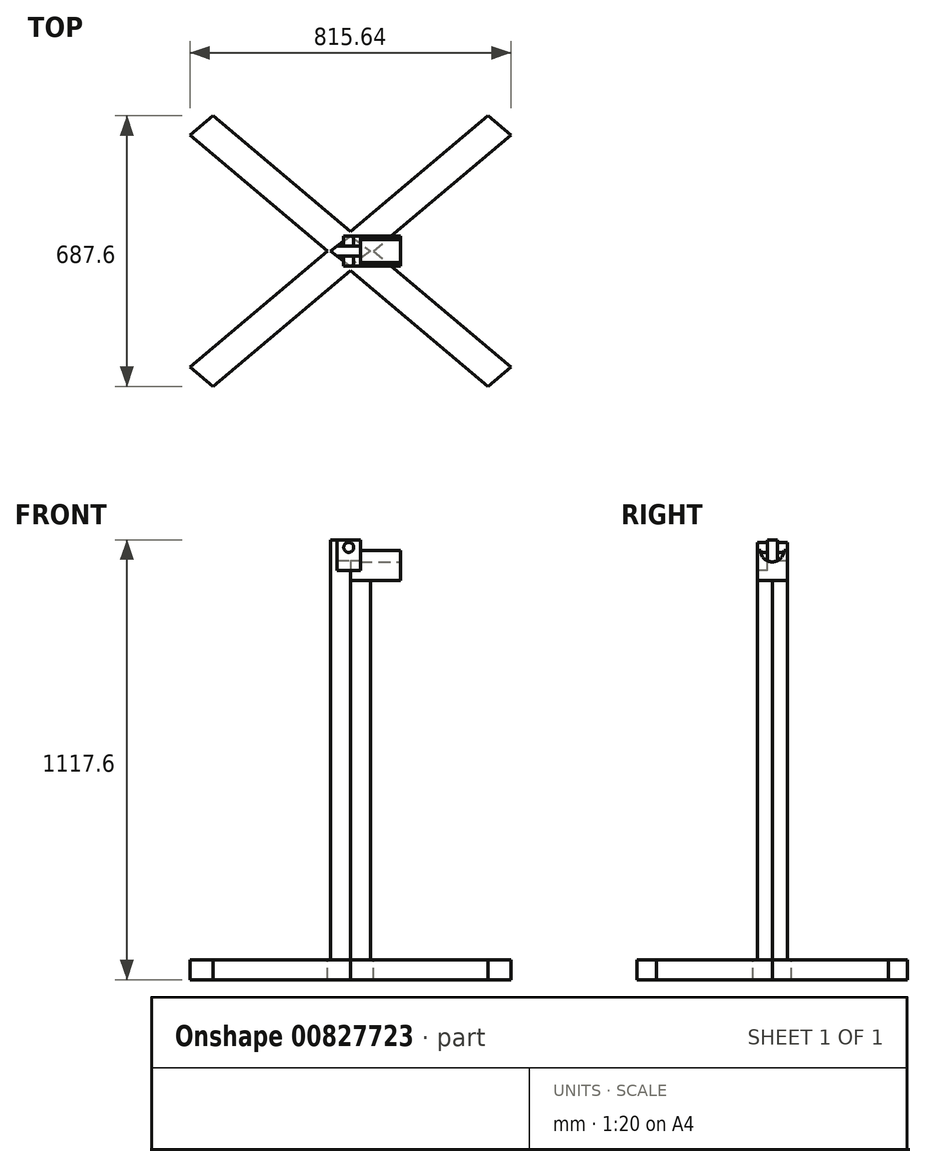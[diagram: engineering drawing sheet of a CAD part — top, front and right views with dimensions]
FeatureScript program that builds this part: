
annotation { "Feature Type Name" : "Feature", "Feature Type Description" : "" }
export const myFeature = defineFeature(function(context is Context, id is Id, definition is map)
    precondition{}
    {
        {
            var Q0;
            Q0=qCreatedBy(makeId("Top.planeOp"),FACE);
            var sketch = newSketch(context, id + "F0", { "sketchPlane" : qUnion([Q0])});
            skPoint(sketch, "E0.middle", {"position": v(0, 0) * mm});
            skLineSegment(sketch, "E1", {"start": v(282.37, -288.57) * mm, "end": v(-67.19, 6.12) * mm});
            skLineSegment(sketch, "E2", {"start": v(-475.01, 349.91) * mm, "end": v(-416.75, 399.03) * mm});
            skLineSegment(sketch, "E3", {"start": v(-416.75, 399.03) * mm, "end": v(-67.19, 104.34) * mm});
            skLineSegment(sketch, "E4", {"start": v(-475.01, -239.45) * mm, "end": v(-416.75, -288.57) * mm});
            skLineSegment(sketch, "E5", {"start": v(-416.75, -288.57) * mm, "end": v(-67.19, 6.12) * mm});
            skLineSegment(sketch, "E6", {"start": v(340.63, 349.91) * mm, "end": v(282.37, 399.03) * mm});
            skLineSegment(sketch, "E7", {"start": v(282.37, 399.03) * mm, "end": v(-67.19, 104.34) * mm});
            skLineSegment(sketch, "E8", {"start": v(282.37, -288.57) * mm, "end": v(340.63, -239.45) * mm});
            skLineSegment(sketch, "E9.trimOffspring", {"start": v(-8.93, 55.23) * mm, "end": v(340.63, -239.45) * mm});
            skLineSegment(sketch, "E10.trimOffspring", {"start": v(-125.45, 55.23) * mm, "end": v(-475.01, -239.45) * mm});
            skLineSegment(sketch, "E11.trimOffspring", {"start": v(-125.45, 55.23) * mm, "end": v(-475.01, 349.91) * mm});
            skLineSegment(sketch, "E12.trimOffspring", {"start": v(-8.93, 55.23) * mm, "end": v(340.63, 349.91) * mm});
            skSolve(sketch);
        }
        {
            var Q0;
            Q0=qSketchRegion(id+"F0",true);
            extrude(context, id + "F1", {"entities" : qUnion([Q0]), "oppositeDirection" : true, "depth" : 50.8 * mm, "offsetDistance" : 25.4 * mm});
        }
        {
            var Q0;
            Q0=makeQuery(id+"F1.opExtrude","CAP_FACE",FACE,{"disambiguationData":[OSD([sQuery(id+"F0.wireOp",EDGE,"E1"),sQuery(id+"F0.wireOp",EDGE,"E2"),sQuery(id+"F0.wireOp",EDGE,"E3"),sQuery(id+"F0.wireOp",EDGE,"E4"),sQuery(id+"F0.wireOp",EDGE,"E5"),sQuery(id+"F0.wireOp",EDGE,"E6"),sQuery(id+"F0.wireOp",EDGE,"E7"),sQuery(id+"F0.wireOp",EDGE,"E8"),sQuery(id+"F0.wireOp",EDGE,"E9.trimOffspring"),sQuery(id+"F0.wireOp",EDGE,"E10.trimOffspring"),sQuery(id+"F0.wireOp",EDGE,"E11.trimOffspring"),sQuery(id+"F0.wireOp",EDGE,"E12.trimOffspring")])],"isStart":true});
            var sketch = newSketch(context, id + "F2", { "sketchPlane" : qUnion([Q0])});
            skLineSegment(sketch, "E13", {"start": v(-125.45, 55.23) * mm, "end": v(-8.93, 55.23) * mm, "construction": true});
            skLineSegment(sketch, "E14", {"start": v(-67.19, 104.34) * mm, "end": v(-67.19, 6.12) * mm, "construction": true});
            skPoint(sketch, "E15.middle", {"position": v(-67.19, 55.23) * mm});
            skLineSegment(sketch, "E16", {"start": v(-117.99, 55.23) * mm, "end": v(-67.19, 93.33) * mm});
            skLineSegment(sketch, "E17", {"start": v(-67.19, 93.33) * mm, "end": v(-16.39, 55.23) * mm});
            skLineSegment(sketch, "E18", {"start": v(-16.39, 55.23) * mm, "end": v(-67.19, 17.13) * mm});
            skLineSegment(sketch, "E19", {"start": v(-67.19, 17.13) * mm, "end": v(-117.99, 55.23) * mm});
            skSolve(sketch);
        }
        {
            var Q0;
            {var subQ0=sQuery(id+"F2.wireOp",EDGE,"wgdWIPvC-I4hR-T0Zt-xnxe-Nl3ozaKQzP4W");var subQ1=makeQuery(id+"F2.imprint","INTERSECT",VERTEX,{"derivedFrom":[makeQuery(id+"F1.opExtrude","CAP_EDGE",EDGE,{"disambiguationData":[OSD([sQuery(id+"F0.wireOp",EDGE,"E1")])],"isStart":true}),makeQuery(id+"F1.opExtrude","CAP_EDGE",EDGE,{"disambiguationData":[OSD([sQuery(id+"F0.wireOp",EDGE,"E5")])],"isStart":true}),subQ0]});Q0=makeQuery(id+"F2.imprint","IMPRINT",FACE,{"disambiguationData":[TD([[makeQuery(id+"F2.imprint","IMPRINT",EDGE,{"disambiguationData":[TD([[subQ1,1.0]])],"derivedFrom":subQ0}),1.0]])]});}
            var Q1;
            Q1=makeQuery(id+"F2.imprint","IMPRINT",FACE,{"disambiguationData":[TD([[makeQuery(id+"F2.imprint","IMPRINT",EDGE,{"derivedFrom":sQuery(id+"F2.wireOp",EDGE,"VLmX2QcA-QAkb-Bhdo-7lbi-0TtQg2hfHBJQ")}),-1.0]])]});
            var Q2;
            Q2=makeQuery(id+"F2.imprint","IMPRINT",FACE,{"disambiguationData":[TD([[makeQuery(id+"F2.imprint","IMPRINT",EDGE,{"derivedFrom":sQuery(id+"F2.wireOp",EDGE,"E16")}),-1.0]])]});
            extrude(context, id + "F3", {"entities" : qUnion([Q0, Q1, Q2]), "operationType" : NewBodyOperationType.ADD, "depth" : 1066.8 * mm, "offsetDistance" : 25.4 * mm});
        }
        {
            var Q0;
            Q0=makeQuery(id+"F3.opExtrude","CAP_FACE",FACE,{"disambiguationData":[OSD([sQuery(id+"F2.wireOp",EDGE,"E16"),sQuery(id+"F2.wireOp",EDGE,"E17"),sQuery(id+"F2.wireOp",EDGE,"E18"),sQuery(id+"F2.wireOp",EDGE,"E19")])],"isStart":false});
            var sketch = newSketch(context, id + "F4", { "sketchPlane" : qUnion([Q0])});
            skLineSegment(sketch, "E20.top", {"start": v(-28.53, 103.17) * mm, "end": v(-104.72, 103.17) * mm});
            skLineSegment(sketch, "E20.left", {"start": v(-28.53, 67.93) * mm, "end": v(-28.53, 103.17) * mm});
            skLineSegment(sketch, "E20.right", {"start": v(-104.72, 67.93) * mm, "end": v(-104.72, 103.17) * mm});
            skLineSegment(sketch, "E21.bottom", {"start": v(-104.45, 42.53) * mm, "end": v(-29.62, 42.53) * mm});
            skLineSegment(sketch, "E21.top", {"start": v(-104.45, 3.33) * mm, "end": v(-29.62, 3.33) * mm});
            skLineSegment(sketch, "E21.left", {"start": v(-104.45, 42.53) * mm, "end": v(-104.45, 3.33) * mm});
            skLineSegment(sketch, "E21.right", {"start": v(-29.62, 42.53) * mm, "end": v(-29.62, 3.33) * mm});
            skLineSegment(sketch, "E22", {"start": v(-117.99, 55.23) * mm, "end": v(-16.39, 55.23) * mm, "construction": true});
            skLineSegment(sketch, "E23", {"start": v(-104.72, 67.93) * mm, "end": v(-28.53, 67.93) * mm});
            skSolve(sketch);
        }
        {
            var Q0;
            {var subQ0=sQuery(id+"F4.wireOp",EDGE,"E21.bottom");var subQ1=makeQuery(id+"F3.opExtrude","CAP_EDGE",EDGE,{"disambiguationData":[OSD([sQuery(id+"F2.wireOp",EDGE,"E19")])],"isStart":false});var subQ2=makeQuery(id+"F4.imprint","INTERSECT",VERTEX,{"derivedFrom":[subQ1,subQ0]});Q0=makeQuery(id+"F4.imprint","IMPRINT",FACE,{"disambiguationData":[TD([[makeQuery(id+"F4.imprint","IMPRINT",EDGE,{"disambiguationData":[TD([[subQ2,-1.0]])],"derivedFrom":subQ0}),-1.0]])]});}
            var Q1;
            {var subQ0=sQuery(id+"F4.wireOp",EDGE,"E20.bottom");var subQ1=makeQuery(id+"F3.opExtrude","CAP_EDGE",EDGE,{"disambiguationData":[OSD([sQuery(id+"F2.wireOp",EDGE,"E17")])],"isStart":false});var subQ2=makeQuery(id+"F4.imprint","INTERSECT",VERTEX,{"derivedFrom":[subQ1,subQ0]});Q1=makeQuery(id+"F4.imprint","IMPRINT",FACE,{"disambiguationData":[TD([[makeQuery(id+"F4.imprint","IMPRINT",EDGE,{"disambiguationData":[TD([[subQ2,-1.0]])],"derivedFrom":subQ0}),-1.0]])]});}
            var Q2;
            {var subQ0=sQuery(id+"F4.wireOp",EDGE,"E23");var subQ1=makeQuery(id+"F3.opExtrude","CAP_EDGE",EDGE,{"disambiguationData":[OSD([sQuery(id+"F2.wireOp",EDGE,"E16")])],"isStart":false});var subQ2=makeQuery(id+"F4.imprint","INTERSECT",VERTEX,{"derivedFrom":[subQ1,subQ0]});Q2=makeQuery(id+"F4.imprint","IMPRINT",FACE,{"disambiguationData":[TD([[makeQuery(id+"F4.imprint","IMPRINT",EDGE,{"disambiguationData":[TD([[subQ2,-1.0]])],"derivedFrom":subQ0}),1.0]])]});}
            extrude(context, id + "F5", {"entities" : qUnion([Q0, Q1, Q2]), "operationType" : NewBodyOperationType.REMOVE, "oppositeDirection" : true, "depth" : 26.67 * mm, "offsetDistance" : 25.4 * mm});
        }
        {
            var Q0;
            Q0=makeQuery(id+"F5.boolean.opBoolean","COPY",FACE,{"derivedFrom":makeQuery(id+"F5.opExtrude","CAP_FACE",FACE,{"disambiguationData":[OSD([sQuery(id+"F2.wireOp",EDGE,"E16"),sQuery(id+"F2.wireOp",EDGE,"E17"),sQuery(id+"F4.wireOp",EDGE,"E23")])],"isStart":false})});
            var sketch = newSketch(context, id + "F6", { "sketchPlane" : qUnion([Q0])});
            skLineSegment(sketch, "E24.0", {"start": v(-67.19, 93.33) * mm, "end": v(-33.32, 67.93) * mm});
            skLineSegment(sketch, "E25.0", {"start": v(-33.32, 67.93) * mm, "end": v(-16.39, 55.23) * mm});
            skLineSegment(sketch, "E26.0", {"start": v(-16.39, 55.23) * mm, "end": v(-33.32, 42.53) * mm});
            skLineSegment(sketch, "E27.0", {"start": v(-33.32, 42.53) * mm, "end": v(-67.19, 17.13) * mm});
            skLineSegment(sketch, "E28.bottom", {"start": v(-67.19, 93.33) * mm, "end": v(59.81, 93.33) * mm});
            skLineSegment(sketch, "E28.top", {"start": v(-67.19, 17.13) * mm, "end": v(59.81, 17.13) * mm});
            skLineSegment(sketch, "E28.right", {"start": v(59.81, 93.33) * mm, "end": v(59.81, 17.13) * mm});
            skSolve(sketch);
        }
        {
            var Q0;
            Q0=makeQuery(id+"F6.imprint","IMPRINT",FACE,{"disambiguationData":[TD([[makeQuery(id+"F6.imprint","IMPRINT",EDGE,{"derivedFrom":sQuery(id+"F6.wireOp",EDGE,"E24.0")}),1.0]])]});
            extrude(context, id + "F7", {"entities" : qUnion([Q0]), "operationType" : NewBodyOperationType.ADD, "oppositeDirection" : true, "depth" : 76.2 * mm, "offsetDistance" : 25.4 * mm});
        }
        {
            var Q0;
            Q0=makeQuery(id+"F7.opExtrude","SWEPT_FACE",FACE,{"disambiguationData":[OSD([sQuery(id+"F6.wireOp",EDGE,"E28.right")])]});
            var sketch = newSketch(context, id + "F8", { "sketchPlane" : qUnion([Q0])});
            skCircle(sketch, "E29", {"center": v(55.23, 1040.13) * mm, "radius": 29.21 * mm});
            skSolve(sketch);
        }
        {
            var Q0;
            Q0=qSketchRegion(id+"F8",true);
            extrude(context, id + "F9", {"entities" : qUnion([Q0]), "operationType" : NewBodyOperationType.REMOVE, "oppositeDirection" : true, "depth" : 101.6 * mm, "offsetDistance" : 25.4 * mm});
        }
        {
            var Q0;
            Q0=makeQuery(id+"F3.opExtrude","CAP_FACE",FACE,{"disambiguationData":[OSD([sQuery(id+"F2.wireOp",EDGE,"E16"),sQuery(id+"F2.wireOp",EDGE,"E17"),sQuery(id+"F2.wireOp",EDGE,"E18"),sQuery(id+"F2.wireOp",EDGE,"E19")])],"isStart":false});
            var sketch = newSketch(context, id + "F10", { "sketchPlane" : qUnion([Q0])});
            skLineSegment(sketch, "E30.0", {"start": v(-41.79, 67.93) * mm, "end": v(-33.32, 67.93) * mm});
            skLineSegment(sketch, "E31.0", {"start": v(-33.32, 67.93) * mm, "end": v(-16.39, 55.23) * mm});
            skLineSegment(sketch, "E32.0", {"start": v(-16.39, 55.23) * mm, "end": v(-33.32, 42.53) * mm});
            skLineSegment(sketch, "E33.0", {"start": v(-41.79, 42.53) * mm, "end": v(-33.32, 42.53) * mm});
            skLineSegment(sketch, "E34", {"start": v(-41.79, 67.93) * mm, "end": v(-41.79, 42.53) * mm});
            skPoint(sketch, "E35.orphan", {"position": v(-101.06, 67.93) * mm});
            skPoint(sketch, "E36.orphan", {"position": v(-101.06, 42.53) * mm});
            skPoint(sketch, "E37.0.end.orphan", {"position": v(-41.79, 84.44) * mm});
            skSolve(sketch);
        }
        {
            var Q0;
            Q0=makeQuery(id+"F10.imprint","IMPRINT",FACE,{"disambiguationData":[TD([[makeQuery(id+"F10.imprint","IMPRINT",EDGE,{"derivedFrom":sQuery(id+"F10.wireOp",EDGE,"E30.0")}),-1.0]])]});
            var Q1;
            {var subQ0=sQuery(id+"F10.wireOp",EDGE,"E33.0");Q1=makeQuery(id+"F10.imprint","IMPRINT",FACE,{"disambiguationData":[TD([[makeQuery(id+"F10.imprint","IMPRINT",EDGE,{"derivedFrom":subQ0}),1.0]])]});}
            extrude(context, id + "F11", {"entities" : qUnion([Q0, Q1]), "operationType" : NewBodyOperationType.REMOVE, "endBound" : BoundingType.UP_TO_NEXT, "oppositeDirection" : true, "depth" : 50.8 * mm, "offsetDistance" : 25.4 * mm});
        }
        {
            var Q0;
            Q0=makeQuery(id+"F9.boolean.opBoolean","COPY",FACE,{"derivedFrom":makeQuery(id+"F9.opExtrude","CAP_FACE",FACE,{"disambiguationData":[OSD([sQuery(id+"F8.wireOp",EDGE,"E29")])],"isStart":false})});
            var sketch = newSketch(context, id + "F12", { "sketchPlane" : qUnion([Q0])});
            skLineSegment(sketch, "E38.0", {"start": v(26.02, 1040.13) * mm, "end": v(42.53, 1040.13) * mm});
            skLineSegment(sketch, "E39.0", {"start": v(67.93, 1040.13) * mm, "end": v(84.44, 1040.13) * mm});
            skArc(sketch, "E40.0", {"start": v(26.02, 1040.13) * mm, "mid": v(30.49, 1024.6) * mm, "end": v(42.53, 1013.83) * mm});
            skLineSegment(sketch, "E41", {"start": v(42.53, 1040.13) * mm, "end": v(42.53, 1013.83) * mm});
            skLineSegment(sketch, "E42", {"start": v(67.93, 1040.13) * mm, "end": v(67.93, 1013.83) * mm});
            skArc(sketch, "E43.trimOffspring", {"start": v(67.93, 1013.83) * mm, "mid": v(79.97, 1024.6) * mm, "end": v(84.44, 1040.13) * mm});
            skSolve(sketch);
        }
        {
            var Q0;
            Q0=qSketchRegion(id+"F12",true);
            extrude(context, id + "F13", {"entities" : qUnion([Q0]), "operationType" : NewBodyOperationType.REMOVE, "endBound" : BoundingType.UP_TO_NEXT, "oppositeDirection" : true, "depth" : 25.4 * mm, "offsetDistance" : 25.4 * mm});
        }
        {
            var Q0;
            Q0=makeQuery(id+"F7.opExtrude","SWEPT_FACE",FACE,{"disambiguationData":[OSD([sQuery(id+"F6.wireOp",EDGE,"E28.top")])]});
            var sketch = newSketch(context, id + "F14", { "sketchPlane" : qUnion([Q0])});
            skLineSegment(sketch, "E44.0", {"start": v(-67.19, 1040.13) * mm, "end": v(-41.79, 1040.13) * mm});
            skPoint(sketch, "E45.orphan", {"position": v(59.81, 1040.13) * mm});
            skPoint(sketch, "E46.orphan", {"position": v(-41.79, 1066.8) * mm});
            skLineSegment(sketch, "E47", {"start": v(-67.19, 1040.13) * mm, "end": v(-101.06, 1040.13) * mm});
            skPoint(sketch, "E48.orphan", {"position": v(-101.06, 1066.8) * mm});
            skLineSegment(sketch, "E49.top", {"start": v(-101.06, 989.33) * mm, "end": v(-41.79, 989.33) * mm});
            skLineSegment(sketch, "E50", {"start": v(-101.06, 989.33) * mm, "end": v(-101.06, 1040.13) * mm});
            skLineSegment(sketch, "E51", {"start": v(-41.79, 989.33) * mm, "end": v(-41.79, 1040.13) * mm});
            skSolve(sketch);
        }
        {
            var Q0;
            {var subQ0=sQuery(id+"F14.wireOp",EDGE,"91e3f64d-cfc5-48aa-956f-56200beb85da.0");Q0=makeQuery(id+"F14.imprint","IMPRINT",FACE,{"disambiguationData":[TD([[makeQuery(id+"F14.imprint","IMPRINT",EDGE,{"derivedFrom":subQ0}),-1.0]])]});}
            var Q1;
            {var subQ0=sQuery(id+"F14.wireOp",EDGE,"3b4ab840-8c4a-4b07-9c90-480e8c33c28e.0");Q1=makeQuery(id+"F14.imprint","IMPRINT",FACE,{"disambiguationData":[TD([[makeQuery(id+"F14.imprint","IMPRINT",EDGE,{"derivedFrom":subQ0}),1.0]])]});}
            var Q2;
            {var subQ0=sQuery(id+"F14.wireOp",EDGE,"E47");Q2=makeQuery(id+"F14.imprint","IMPRINT",FACE,{"disambiguationData":[TD([[makeQuery(id+"F14.imprint","IMPRINT",EDGE,{"derivedFrom":subQ0}),1.0]])]});}
            var Q3;
            {var subQ0=sQuery(id+"F14.wireOp",EDGE,"E44.0");Q3=makeQuery(id+"F14.imprint","IMPRINT",FACE,{"disambiguationData":[TD([[makeQuery(id+"F14.imprint","IMPRINT",EDGE,{"derivedFrom":subQ0}),-1.0]])]});}
            var Q4;
            Q4=makeQuery(id+"F13.boolean.opBoolean","MERGE",FACE,{"derivedFrom":[makeQuery(id+"F5.boolean.opBoolean","COPY",FACE,{"derivedFrom":makeQuery(id+"F5.opExtrude","SWEPT_FACE",FACE,{"disambiguationData":[OSD([sQuery(id+"F4.wireOp",EDGE,"E21.bottom")])]})}),makeQuery(id+"F13.opExtrude","SWEPT_FACE",FACE,{"disambiguationData":[OSD([sQuery(id+"F12.wireOp",EDGE,"E41")])]})]});
            extrude(context, id + "F15", {"entities" : qUnion([Q0, Q1, Q2, Q3]), "operationType" : NewBodyOperationType.REMOVE, "oppositeDirection" : true, "depth" : 25.4 * mm, "endBoundEntityFace" : qUnion([Q4]), "offsetDistance" : 25.4 * mm});
        }
        {
            var Q0;
            Q0=makeQuery(id+"F7.opExtrude","SWEPT_FACE",FACE,{"disambiguationData":[OSD([sQuery(id+"F6.wireOp",EDGE,"E28.bottom")])]});
            var sketch = newSketch(context, id + "F16", { "sketchPlane" : qUnion([Q0])});
            skLineSegment(sketch, "E52.0", {"start": v(41.79, 1013.83) * mm, "end": v(41.79, 1040.13) * mm});
            skLineSegment(sketch, "E53.0", {"start": v(101.06, 1013.83) * mm, "end": v(41.79, 1013.83) * mm});
            skLineSegment(sketch, "E54.0", {"start": v(101.06, 1013.83) * mm, "end": v(101.06, 1040.13) * mm});
            skLineSegment(sketch, "E55.0", {"start": v(67.19, 1040.13) * mm, "end": v(41.79, 1040.13) * mm});
            skLineSegment(sketch, "E56", {"start": v(67.19, 1040.13) * mm, "end": v(101.06, 1040.13) * mm});
            skPoint(sketch, "E57.orphan", {"position": v(41.79, 1066.8) * mm});
            skPoint(sketch, "E58.orphan", {"position": v(101.06, 1066.8) * mm});
            skPoint(sketch, "E59.orphan", {"position": v(-59.81, 1040.13) * mm});
            skSolve(sketch);
        }
        {
            var Q0;
            {var subQ0=sQuery(id+"F16.wireOp",EDGE,"E54.0");Q0=makeQuery(id+"F16.imprint","IMPRINT",FACE,{"disambiguationData":[TD([[makeQuery(id+"F16.imprint","IMPRINT",EDGE,{"derivedFrom":subQ0}),1.0]])]});}
            var Q1;
            {var subQ0=sQuery(id+"F16.wireOp",EDGE,"E52.0");Q1=makeQuery(id+"F16.imprint","IMPRINT",FACE,{"disambiguationData":[TD([[makeQuery(id+"F16.imprint","IMPRINT",EDGE,{"derivedFrom":subQ0}),-1.0]])]});}
            extrude(context, id + "F17", {"entities" : qUnion([Q0, Q1]), "operationType" : NewBodyOperationType.REMOVE, "oppositeDirection" : true, "depth" : 25.4 * mm, "offsetDistance" : 25.4 * mm});
        }
        {
            var Q0;
            Q0=makeQuery(id+"F13.boolean.opBoolean","MERGE",FACE,{"derivedFrom":[makeQuery(id+"F5.boolean.opBoolean","COPY",FACE,{"derivedFrom":makeQuery(id+"F5.opExtrude","SWEPT_FACE",FACE,{"disambiguationData":[OSD([sQuery(id+"F4.wireOp",EDGE,"E21.bottom")])]})}),makeQuery(id+"F13.opExtrude","SWEPT_FACE",FACE,{"disambiguationData":[OSD([sQuery(id+"F12.wireOp",EDGE,"E41")])]})]});
            var sketch = newSketch(context, id + "F18", { "sketchPlane" : qUnion([Q0])});
            skCircle(sketch, "E60", {"center": v(-71.42, 1047.75) * mm, "radius": 12.7 * mm});
            skPoint(sketch, "E60.centerSnap0", {"position": v(-71.42, 1066.8) * mm});
            skSolve(sketch);
        }
        {
            var Q0;
            Q0=makeQuery(id+"F18.imprint","IMPRINT",FACE,{"disambiguationData":[TD([[makeQuery(id+"F18.imprint","IMPRINT",EDGE,{"derivedFrom":sQuery(id+"F18.wireOp",EDGE,"E60")}),1.0]])]});
            extrude(context, id + "F19", {"entities" : qUnion([Q0]), "operationType" : NewBodyOperationType.ADD, "depth" : 25.4 * mm, "offsetDistance" : 25.4 * mm, "hasSecondDirection" : true, "secondDirectionOppositeDirection" : true, "secondDirectionDepth" : 50.8 * mm});
        }
    });
